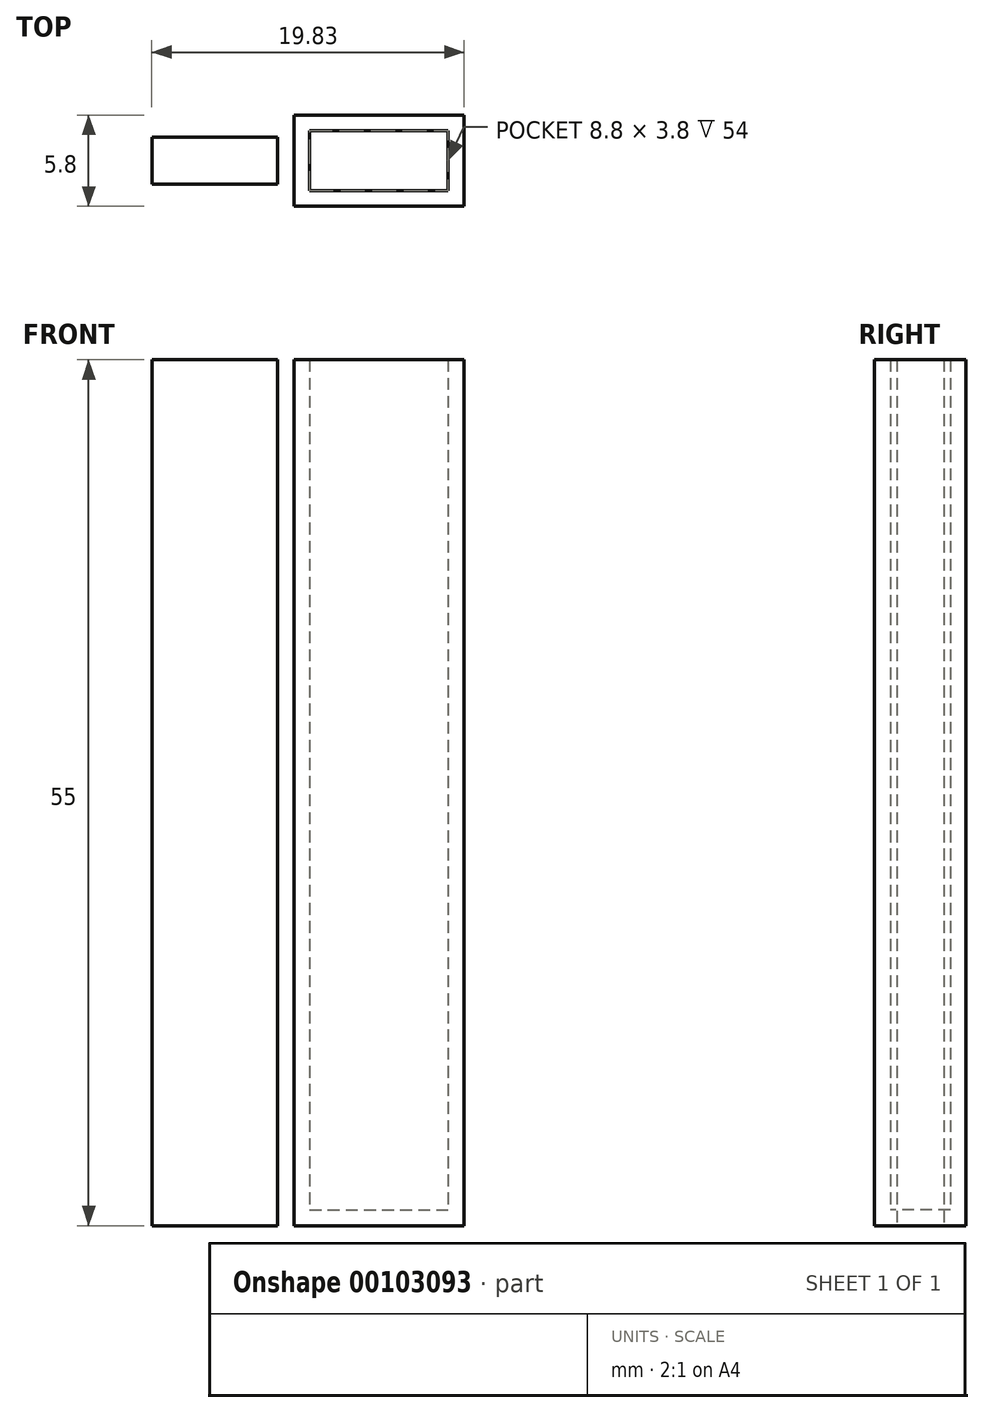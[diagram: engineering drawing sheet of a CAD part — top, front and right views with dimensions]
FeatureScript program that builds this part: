
annotation { "Feature Type Name" : "Feature", "Feature Type Description" : "" }
export const myFeature = defineFeature(function(context is Context, id is Id, definition is map)
    precondition{}
    {
        {
            var Q0;
            Q0=qCreatedBy(makeId("Top.planeOp"),FACE);
            var sketch = newSketch(context, id + "F0", { "sketchPlane" : qUnion([Q0])});
            skLineSegment(sketch, "E0.bottom", {"start": v(-11.53, 0) * mm, "end": v(-3.53, 0) * mm});
            skLineSegment(sketch, "E0.top", {"start": v(-11.53, 3) * mm, "end": v(-3.53, 3) * mm});
            skLineSegment(sketch, "E0.left", {"start": v(-11.53, 0) * mm, "end": v(-11.53, 3) * mm});
            skLineSegment(sketch, "E0.right", {"start": v(-3.53, 0) * mm, "end": v(-3.53, 3) * mm});
            skLineSegment(sketch, "E1.bottom", {"start": v(-1.1, 3) * mm, "end": v(6.9, 3) * mm, "construction": true});
            skLineSegment(sketch, "E1.top", {"start": v(-1.1, 0) * mm, "end": v(6.9, 0) * mm, "construction": true});
            skLineSegment(sketch, "E1.left", {"start": v(-1.1, 3) * mm, "end": v(-1.1, 0) * mm, "construction": true});
            skLineSegment(sketch, "E1.right", {"start": v(6.9, 3) * mm, "end": v(6.9, 0) * mm, "construction": true});
            skLineSegment(sketch, "E2.0", {"start": v(-2.5, -1.4) * mm, "end": v(8.3, -1.4) * mm});
            skLineSegment(sketch, "E2.1", {"start": v(-2.5, 4.4) * mm, "end": v(-2.5, -1.4) * mm});
            skLineSegment(sketch, "E2.2", {"start": v(-2.5, 4.4) * mm, "end": v(8.3, 4.4) * mm});
            skLineSegment(sketch, "E2.3", {"start": v(8.3, 4.4) * mm, "end": v(8.3, -1.4) * mm});
            skSolve(sketch);
        }
        {
            var Q0;
            Q0 = qSketchRegion(id + "F0", true);
            var Q1;
            Q1=sQuery(id+"F0.wireOp",EDGE,"nauhSgGS-zy9I-HaWY-opW2-mhqk7vYS6UTa.right");
            var Q2;
            Q2=sQuery(id+"F0.wireOp",EDGE,"nauhSgGS-zy9I-HaWY-opW2-mhqk7vYS6UTa.top");
            var Q3;
            Q3=sQuery(id+"F0.wireOp",EDGE,"nauhSgGS-zy9I-HaWY-opW2-mhqk7vYS6UTa.left");
            var Q4;
            Q4=sQuery(id+"F0.wireOp",EDGE,"nauhSgGS-zy9I-HaWY-opW2-mhqk7vYS6UTa.bottom");
            extrude(context, id + "F1", {"entities" : qUnion([Q0]), "surfaceEntities" : qUnion([Q1, Q2, Q3, Q4]), "depth" : 55 * mm});
        }
        {
            var Q0;
            Q0=makeQuery(id+"F1.opExtrude","CAP_FACE",FACE,{"disambiguationData":[OSD([sQuery(id+"F0.wireOp",EDGE,"E2.0"),sQuery(id+"F0.wireOp",EDGE,"E2.1"),sQuery(id+"F0.wireOp",EDGE,"E2.2"),sQuery(id+"F0.wireOp",EDGE,"E2.3")])],"isStart":false});
            shell(context, id + "F2", {"entities" : qUnion([Q0]), "thickness" : 1 * mm});
        }
    });
